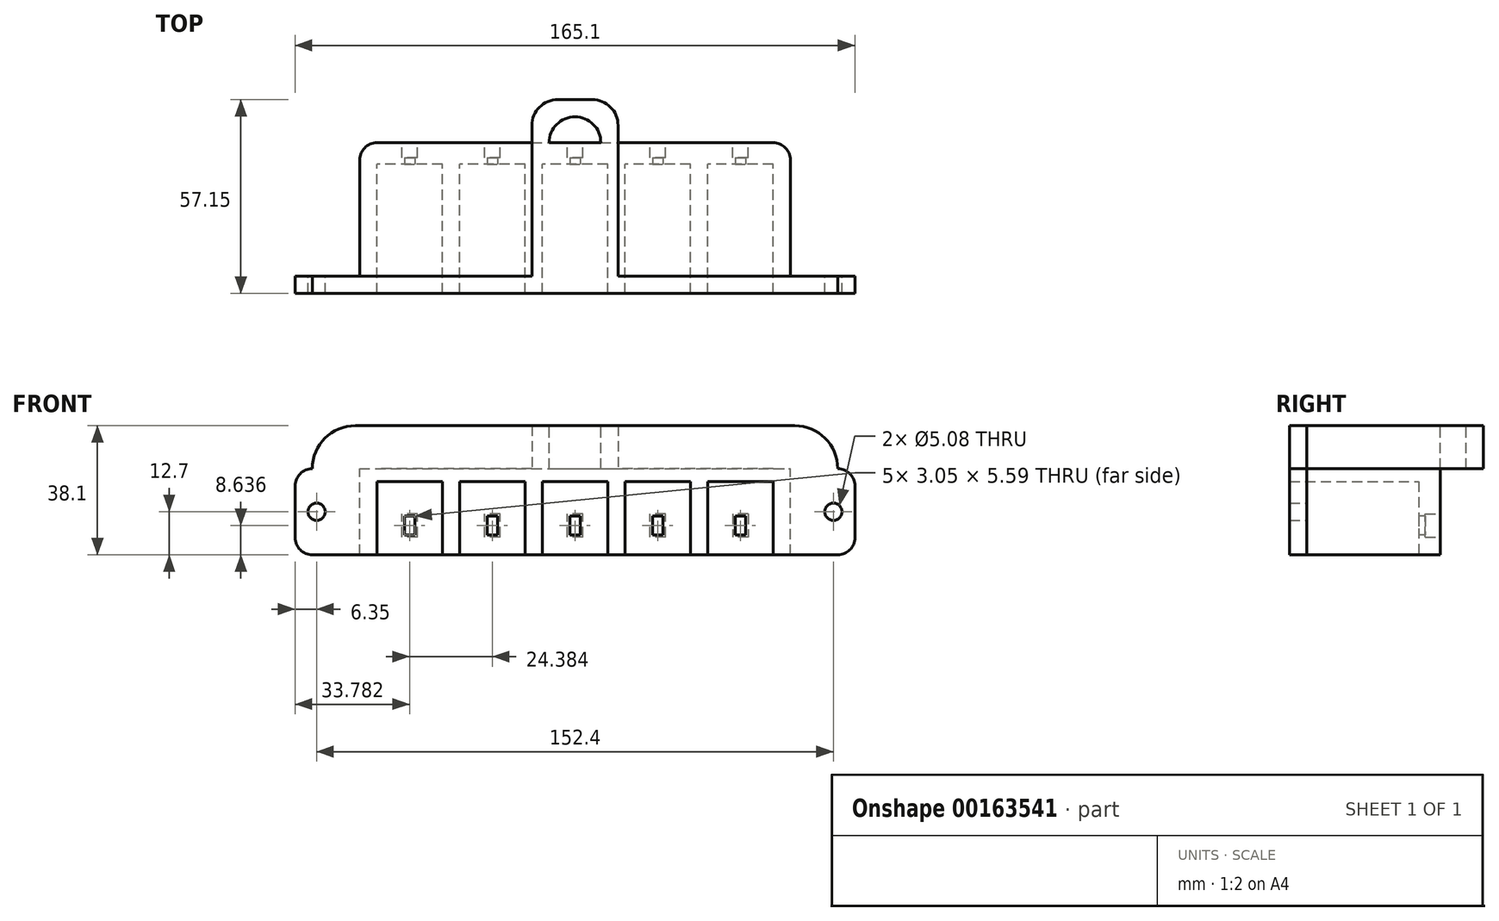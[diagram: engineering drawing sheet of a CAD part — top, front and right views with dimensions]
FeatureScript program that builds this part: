
annotation { "Feature Type Name" : "Feature", "Feature Type Description" : "" }
export const myFeature = defineFeature(function(context is Context, id is Id, definition is map)
    precondition{}
    {
        {
            var Q0;
            Q0=qCreatedBy(makeId("Front.planeOp"),FACE);
            var sketch = newSketch(context, id + "F0", { "sketchPlane" : qUnion([Q0])});
            skLineSegment(sketch, "E0.bottom", {"start": v(0, 0) * mm, "end": v(-127, 0) * mm});
            skLineSegment(sketch, "E0.top", {"start": v(0, 25.4) * mm, "end": v(-127, 25.4) * mm});
            skLineSegment(sketch, "E0.left", {"start": v(0, 0) * mm, "end": v(0, 25.4) * mm});
            skLineSegment(sketch, "E0.right", {"start": v(-127, 0) * mm, "end": v(-127, 25.4) * mm});
            skSolve(sketch);
        }
        {
            var Q0;
            Q0=makeQuery(id+"F0.imprint","IMPRINT",FACE,{"disambiguationData":[TD([[makeQuery(id+"F0.imprint","IMPRINT",EDGE,{"derivedFrom":sQuery(id+"F0.wireOp",EDGE,"E0.bottom")}),-1.0]])]});
            extrude(context, id + "F1", {"entities" : qUnion([Q0]), "depth" : 6.35 * mm});
        }
        {
            var Q0;
            Q0=makeQuery(id+"F1.opExtrude","CAP_FACE",FACE,{"disambiguationData":[OSD([sQuery(id+"F0.wireOp",EDGE,"E0.bottom"),sQuery(id+"F0.wireOp",EDGE,"E0.top"),sQuery(id+"F0.wireOp",EDGE,"E0.left"),sQuery(id+"F0.wireOp",EDGE,"E0.right")])],"isStart":false});
            var sketch = newSketch(context, id + "F2", { "sketchPlane" : qUnion([Q0])});
            skLineSegment(sketch, "E1.bottom", {"start": v(-127, 25.4) * mm, "end": v(-121.92, 25.4) * mm});
            skLineSegment(sketch, "E1.top", {"start": v(-127, 0) * mm, "end": v(-121.92, 0) * mm});
            skLineSegment(sketch, "E1.left", {"start": v(-127, 25.4) * mm, "end": v(-127, 0) * mm});
            skLineSegment(sketch, "E1.right", {"start": v(-121.92, 25.4) * mm, "end": v(-121.92, 0) * mm});
            skLineSegment(sketch, "E2.bottom", {"start": v(-102.62, 25.4) * mm, "end": v(-97.54, 25.4) * mm});
            skLineSegment(sketch, "E2.top", {"start": v(-102.62, 0) * mm, "end": v(-97.54, 0) * mm});
            skLineSegment(sketch, "E2.left", {"start": v(-102.62, 25.4) * mm, "end": v(-102.62, 0) * mm});
            skLineSegment(sketch, "E2.right", {"start": v(-97.54, 25.4) * mm, "end": v(-97.54, 0) * mm});
            skLineSegment(sketch, "E3.bottom", {"start": v(-78.23, 25.4) * mm, "end": v(-73.15, 25.4) * mm});
            skLineSegment(sketch, "E3.top", {"start": v(-78.23, 0) * mm, "end": v(-73.15, 0) * mm});
            skLineSegment(sketch, "E3.left", {"start": v(-78.23, 25.4) * mm, "end": v(-78.23, 0) * mm});
            skLineSegment(sketch, "E3.right", {"start": v(-73.15, 25.4) * mm, "end": v(-73.15, 0) * mm});
            skLineSegment(sketch, "E4.bottom", {"start": v(-53.85, 25.4) * mm, "end": v(-48.77, 25.4) * mm});
            skLineSegment(sketch, "E4.top", {"start": v(-53.85, 0) * mm, "end": v(-48.77, 0) * mm});
            skLineSegment(sketch, "E4.left", {"start": v(-53.85, 25.4) * mm, "end": v(-53.85, 0) * mm});
            skLineSegment(sketch, "E4.right", {"start": v(-48.77, 25.4) * mm, "end": v(-48.77, 0) * mm});
            skLineSegment(sketch, "E5.bottom", {"start": v(-29.46, 25.4) * mm, "end": v(-24.38, 25.4) * mm});
            skLineSegment(sketch, "E5.top", {"start": v(-29.46, 0) * mm, "end": v(-24.38, 0) * mm});
            skLineSegment(sketch, "E5.left", {"start": v(-29.46, 25.4) * mm, "end": v(-29.46, 0) * mm});
            skLineSegment(sketch, "E5.right", {"start": v(-24.38, 25.4) * mm, "end": v(-24.38, 0) * mm});
            skLineSegment(sketch, "E6.bottom", {"start": v(0, 25.4) * mm, "end": v(-5.08, 25.4) * mm});
            skLineSegment(sketch, "E6.top", {"start": v(0, 0) * mm, "end": v(-5.08, 0) * mm});
            skLineSegment(sketch, "E6.left", {"start": v(0, 25.4) * mm, "end": v(0, 0) * mm});
            skLineSegment(sketch, "E6.right", {"start": v(-5.08, 25.4) * mm, "end": v(-5.08, 0) * mm});
            skLineSegment(sketch, "E7.bottom", {"start": v(-5.08, 25.4) * mm, "end": v(-24.38, 25.4) * mm});
            skLineSegment(sketch, "E7.top", {"start": v(-5.08, 21.59) * mm, "end": v(-24.38, 21.59) * mm});
            skLineSegment(sketch, "E7.left", {"start": v(-5.08, 25.4) * mm, "end": v(-5.08, 21.59) * mm});
            skLineSegment(sketch, "E7.right", {"start": v(-24.38, 25.4) * mm, "end": v(-24.38, 21.59) * mm});
            skLineSegment(sketch, "E8.bottom", {"start": v(-29.46, 25.4) * mm, "end": v(-48.77, 25.4) * mm});
            skLineSegment(sketch, "E8.top", {"start": v(-29.46, 21.59) * mm, "end": v(-48.77, 21.59) * mm});
            skLineSegment(sketch, "E8.left", {"start": v(-29.46, 25.4) * mm, "end": v(-29.46, 21.59) * mm});
            skLineSegment(sketch, "E8.right", {"start": v(-48.77, 25.4) * mm, "end": v(-48.77, 21.59) * mm});
            skLineSegment(sketch, "E9.bottom", {"start": v(-53.85, 25.4) * mm, "end": v(-73.15, 25.4) * mm});
            skLineSegment(sketch, "E9.top", {"start": v(-53.85, 21.59) * mm, "end": v(-73.15, 21.59) * mm});
            skLineSegment(sketch, "E9.left", {"start": v(-53.85, 25.4) * mm, "end": v(-53.85, 21.59) * mm});
            skLineSegment(sketch, "E9.right", {"start": v(-73.15, 25.4) * mm, "end": v(-73.15, 21.59) * mm});
            skLineSegment(sketch, "E10.bottom", {"start": v(-78.23, 25.4) * mm, "end": v(-97.54, 25.4) * mm});
            skLineSegment(sketch, "E10.top", {"start": v(-78.23, 21.59) * mm, "end": v(-97.54, 21.59) * mm});
            skLineSegment(sketch, "E10.left", {"start": v(-78.23, 25.4) * mm, "end": v(-78.23, 21.59) * mm});
            skLineSegment(sketch, "E10.right", {"start": v(-97.54, 25.4) * mm, "end": v(-97.54, 21.59) * mm});
            skLineSegment(sketch, "E11.bottom", {"start": v(-102.62, 25.4) * mm, "end": v(-121.92, 25.4) * mm});
            skLineSegment(sketch, "E11.top", {"start": v(-102.62, 21.59) * mm, "end": v(-121.92, 21.59) * mm});
            skLineSegment(sketch, "E11.left", {"start": v(-102.62, 25.4) * mm, "end": v(-102.62, 21.59) * mm});
            skLineSegment(sketch, "E11.right", {"start": v(-121.92, 25.4) * mm, "end": v(-121.92, 21.59) * mm});
            skSolve(sketch);
        }
        {
            var Q0;
            Q0 = qSketchRegion(id + "F2", true);
            extrude(context, id + "F3", {"entities" : qUnion([Q0]), "operationType" : NewBodyOperationType.ADD, "depth" : 38.1 * mm});
        }
        {
            var Q0;
            {var subQ0=sQuery(id+"F0.wireOp",EDGE,"E0.bottom");Q0=makeQuery(id+"F3.boolean.opBoolean","SPLIT",FACE,{"disambiguationData":[TD([makeQuery(id+"F3.opExtrude","SWEPT_FACE",FACE,{"disambiguationData":[OSD([sQuery(id+"F2.wireOp",EDGE,"E5.right")])]})])],"derivedFrom":makeQuery(id+"F1.opExtrude","CAP_FACE",FACE,{"disambiguationData":[OSD([subQ0,sQuery(id+"F0.wireOp",EDGE,"E0.top"),sQuery(id+"F0.wireOp",EDGE,"E0.left"),sQuery(id+"F0.wireOp",EDGE,"E0.right")])],"isStart":false})});}
            var sketch = newSketch(context, id + "F4", { "sketchPlane" : qUnion([Q0])});
            skPoint(sketch, "E12", {"position": v(-14.73, 8.64) * mm});
            skLineSegment(sketch, "E13.bottom", {"start": v(-16.26, 11.43) * mm, "end": v(-13.2, 11.43) * mm});
            skLineSegment(sketch, "E13.top", {"start": v(-16.26, 5.84) * mm, "end": v(-13.2, 5.84) * mm});
            skLineSegment(sketch, "E13.left", {"start": v(-16.26, 11.43) * mm, "end": v(-16.26, 5.84) * mm});
            skLineSegment(sketch, "E13.right", {"start": v(-13.2, 11.43) * mm, "end": v(-13.2, 5.84) * mm});
            skSolve(sketch);
        }
        {
            var Q0;
            Q0 = qSketchRegion(id + "F4", true);
            extrude(context, id + "F5", {"entities" : qUnion([Q0]), "operationType" : NewBodyOperationType.REMOVE, "endBound" : BoundingType.THROUGH_ALL, "oppositeDirection" : true, "depth" : 5.08 * mm});
        }
        {
            var Q0;
            {var subQ0=sQuery(id+"F0.wireOp",EDGE,"E0.bottom");Q0=makeQuery(id+"F3.boolean.opBoolean","SPLIT",FACE,{"disambiguationData":[TD([makeQuery(id+"F3.opExtrude","SWEPT_FACE",FACE,{"disambiguationData":[OSD([sQuery(id+"F2.wireOp",EDGE,"E4.right")])]})])],"derivedFrom":makeQuery(id+"F1.opExtrude","CAP_FACE",FACE,{"disambiguationData":[OSD([subQ0,sQuery(id+"F0.wireOp",EDGE,"E0.top"),sQuery(id+"F0.wireOp",EDGE,"E0.left"),sQuery(id+"F0.wireOp",EDGE,"E0.right")])],"isStart":false})});}
            var sketch = newSketch(context, id + "F6", { "sketchPlane" : qUnion([Q0])});
            skLineSegment(sketch, "E14.bottom", {"start": v(-40.64, 11.43) * mm, "end": v(-37.6, 11.43) * mm});
            skLineSegment(sketch, "E14.top", {"start": v(-40.64, 5.84) * mm, "end": v(-37.6, 5.84) * mm});
            skLineSegment(sketch, "E14.left", {"start": v(-40.64, 11.43) * mm, "end": v(-40.64, 5.84) * mm});
            skLineSegment(sketch, "E14.right", {"start": v(-37.6, 11.43) * mm, "end": v(-37.6, 5.84) * mm});
            skPoint(sketch, "E14.middle", {"position": v(-39.12, 8.64) * mm});
            skLineSegment(sketch, "E15.bottom", {"start": v(-65.02, 11.43) * mm, "end": v(-61.98, 11.43) * mm});
            skLineSegment(sketch, "E15.top", {"start": v(-65.02, 5.84) * mm, "end": v(-61.98, 5.84) * mm});
            skLineSegment(sketch, "E15.left", {"start": v(-65.02, 11.43) * mm, "end": v(-65.02, 5.84) * mm});
            skLineSegment(sketch, "E15.right", {"start": v(-61.98, 11.43) * mm, "end": v(-61.98, 5.84) * mm});
            skPoint(sketch, "E15.middle", {"position": v(-63.5, 8.64) * mm});
            skLineSegment(sketch, "E16.bottom", {"start": v(-89.4, 11.43) * mm, "end": v(-86.36, 11.43) * mm});
            skLineSegment(sketch, "E16.top", {"start": v(-89.4, 5.84) * mm, "end": v(-86.36, 5.84) * mm});
            skLineSegment(sketch, "E16.left", {"start": v(-89.4, 11.43) * mm, "end": v(-89.4, 5.84) * mm});
            skLineSegment(sketch, "E16.right", {"start": v(-86.36, 11.43) * mm, "end": v(-86.36, 5.84) * mm});
            skPoint(sketch, "E16.middle", {"position": v(-87.88, 8.64) * mm});
            skLineSegment(sketch, "E17.bottom", {"start": v(-113.8, 11.43) * mm, "end": v(-110.74, 11.43) * mm});
            skLineSegment(sketch, "E17.top", {"start": v(-113.8, 5.84) * mm, "end": v(-110.74, 5.84) * mm});
            skLineSegment(sketch, "E17.left", {"start": v(-113.8, 11.43) * mm, "end": v(-113.8, 5.84) * mm});
            skLineSegment(sketch, "E17.right", {"start": v(-110.74, 11.43) * mm, "end": v(-110.74, 5.84) * mm});
            skPoint(sketch, "E17.middle", {"position": v(-112.27, 8.64) * mm});
            skSolve(sketch);
        }
        {
            var Q0;
            Q0 = qSketchRegion(id + "F6", true);
            extrude(context, id + "F7", {"entities" : qUnion([Q0]), "operationType" : NewBodyOperationType.REMOVE, "endBound" : BoundingType.THROUGH_ALL, "oppositeDirection" : true, "depth" : 25.4 * mm});
        }
        {
            var Q0;
            Q0=makeQuery(id+"F1.opExtrude","CAP_FACE",FACE,{"disambiguationData":[OSD([sQuery(id+"F0.wireOp",EDGE,"E0.bottom"),sQuery(id+"F0.wireOp",EDGE,"E0.top"),sQuery(id+"F0.wireOp",EDGE,"E0.left"),sQuery(id+"F0.wireOp",EDGE,"E0.right")])],"isStart":true});
            var sketch = newSketch(context, id + "F8", { "sketchPlane" : qUnion([Q0])});
            skLineSegment(sketch, "E18.0", {"start": v(13.2, 11.43) * mm, "end": v(13.2, 5.84) * mm});
            skLineSegment(sketch, "E18.1", {"start": v(16.26, 11.43) * mm, "end": v(16.26, 5.84) * mm});
            skLineSegment(sketch, "E18.2", {"start": v(16.26, 5.84) * mm, "end": v(13.2, 5.84) * mm});
            skLineSegment(sketch, "E18.3", {"start": v(16.26, 11.43) * mm, "end": v(13.2, 11.43) * mm});
            skLineSegment(sketch, "E19.bottom", {"start": v(12.45, 12.07) * mm, "end": v(17.02, 12.07) * mm});
            skLineSegment(sketch, "E19.top", {"start": v(12.45, 5.2) * mm, "end": v(17.02, 5.2) * mm});
            skLineSegment(sketch, "E19.left", {"start": v(12.45, 12.07) * mm, "end": v(12.45, 5.2) * mm});
            skLineSegment(sketch, "E19.right", {"start": v(17.02, 12.07) * mm, "end": v(17.02, 5.2) * mm});
            skPoint(sketch, "E19.middle", {"position": v(14.73, 8.64) * mm});
            skLineSegment(sketch, "E20.0", {"start": v(40.64, 5.84) * mm, "end": v(37.6, 5.84) * mm});
            skLineSegment(sketch, "E20.1", {"start": v(40.64, 11.43) * mm, "end": v(40.64, 5.84) * mm});
            skLineSegment(sketch, "E20.2", {"start": v(40.64, 11.43) * mm, "end": v(37.6, 11.43) * mm});
            skLineSegment(sketch, "E20.3", {"start": v(37.6, 11.43) * mm, "end": v(37.6, 5.84) * mm});
            skLineSegment(sketch, "E21.0", {"start": v(65.02, 11.43) * mm, "end": v(65.02, 5.84) * mm});
            skLineSegment(sketch, "E21.1", {"start": v(65.02, 5.84) * mm, "end": v(61.98, 5.84) * mm});
            skLineSegment(sketch, "E21.2", {"start": v(61.98, 11.43) * mm, "end": v(61.98, 5.84) * mm});
            skLineSegment(sketch, "E21.3", {"start": v(65.02, 11.43) * mm, "end": v(61.98, 11.43) * mm});
            skLineSegment(sketch, "E22.0", {"start": v(89.4, 5.84) * mm, "end": v(86.36, 5.84) * mm});
            skLineSegment(sketch, "E22.1", {"start": v(89.4, 11.43) * mm, "end": v(89.4, 5.84) * mm});
            skLineSegment(sketch, "E22.2", {"start": v(89.4, 11.43) * mm, "end": v(86.36, 11.43) * mm});
            skLineSegment(sketch, "E22.3", {"start": v(86.36, 11.43) * mm, "end": v(86.36, 5.84) * mm});
            skLineSegment(sketch, "E23.0", {"start": v(113.8, 5.84) * mm, "end": v(110.74, 5.84) * mm});
            skLineSegment(sketch, "E23.1", {"start": v(113.8, 11.43) * mm, "end": v(113.8, 5.84) * mm});
            skLineSegment(sketch, "E23.2", {"start": v(113.8, 11.43) * mm, "end": v(110.74, 11.43) * mm});
            skLineSegment(sketch, "E23.3", {"start": v(110.74, 11.43) * mm, "end": v(110.74, 5.84) * mm});
            skLineSegment(sketch, "E24.bottom", {"start": v(109.98, 5.2) * mm, "end": v(114.55, 5.2) * mm});
            skLineSegment(sketch, "E24.top", {"start": v(109.98, 12.06) * mm, "end": v(114.55, 12.06) * mm});
            skLineSegment(sketch, "E24.left", {"start": v(109.98, 5.2) * mm, "end": v(109.98, 12.06) * mm});
            skLineSegment(sketch, "E24.right", {"start": v(114.55, 5.2) * mm, "end": v(114.55, 12.06) * mm});
            skPoint(sketch, "E24.middle", {"position": v(112.27, 8.64) * mm});
            skLineSegment(sketch, "E25.bottom", {"start": v(85.6, 5.2) * mm, "end": v(90.17, 5.2) * mm});
            skLineSegment(sketch, "E25.top", {"start": v(85.6, 12.06) * mm, "end": v(90.17, 12.06) * mm});
            skLineSegment(sketch, "E25.left", {"start": v(85.6, 5.2) * mm, "end": v(85.6, 12.06) * mm});
            skLineSegment(sketch, "E25.right", {"start": v(90.17, 5.2) * mm, "end": v(90.17, 12.06) * mm});
            skPoint(sketch, "E25.middle", {"position": v(87.88, 8.64) * mm});
            skLineSegment(sketch, "E26.bottom", {"start": v(61.21, 5.2) * mm, "end": v(65.79, 5.2) * mm});
            skLineSegment(sketch, "E26.top", {"start": v(61.21, 12.06) * mm, "end": v(65.79, 12.06) * mm});
            skLineSegment(sketch, "E26.left", {"start": v(61.21, 5.2) * mm, "end": v(61.21, 12.06) * mm});
            skLineSegment(sketch, "E26.right", {"start": v(65.79, 5.2) * mm, "end": v(65.79, 12.06) * mm});
            skPoint(sketch, "E26.middle", {"position": v(63.5, 8.64) * mm});
            skLineSegment(sketch, "E27.bottom", {"start": v(36.83, 5.2) * mm, "end": v(41.4, 5.2) * mm});
            skLineSegment(sketch, "E27.top", {"start": v(36.83, 12.06) * mm, "end": v(41.4, 12.06) * mm});
            skLineSegment(sketch, "E27.left", {"start": v(36.83, 5.2) * mm, "end": v(36.83, 12.06) * mm});
            skLineSegment(sketch, "E27.right", {"start": v(41.4, 5.2) * mm, "end": v(41.4, 12.06) * mm});
            skPoint(sketch, "E27.middle", {"position": v(39.12, 8.64) * mm});
            skSolve(sketch);
        }
        {
            var Q0;
            Q0 = qSketchRegion(id + "F8", true);
            extrude(context, id + "F9", {"entities" : qUnion([Q0]), "operationType" : NewBodyOperationType.REMOVE, "oppositeDirection" : true, "depth" : 4.44 * mm});
        }
        {
            var Q0;
            Q0=makeQuery(id+"F3.boolean.opBoolean","MERGE",FACE,{"derivedFrom":[makeQuery(id+"F1.opExtrude","SWEPT_FACE",FACE,{"disambiguationData":[OSD([sQuery(id+"F0.wireOp",EDGE,"E0.left")])]}),makeQuery(id+"F3.opExtrude","SWEPT_FACE",FACE,{"disambiguationData":[OSD([sQuery(id+"F2.wireOp",EDGE,"E6.left")])]})]});
            var sketch = newSketch(context, id + "F10", { "sketchPlane" : qUnion([Q0])});
            skLineSegment(sketch, "E28.bottom", {"start": v(-44.45, 25.4) * mm, "end": v(-39.37, 25.4) * mm});
            skLineSegment(sketch, "E28.top", {"start": v(-44.45, 0) * mm, "end": v(-39.37, 0) * mm});
            skLineSegment(sketch, "E28.left", {"start": v(-44.45, 25.4) * mm, "end": v(-44.45, 0) * mm});
            skLineSegment(sketch, "E28.right", {"start": v(-39.37, 25.4) * mm, "end": v(-39.37, 0) * mm});
            skSolve(sketch);
        }
        {
            var Q0;
            Q0=makeQuery(id+"F10.imprint","IMPRINT",FACE,{"disambiguationData":[TD([[makeQuery(id+"F10.imprint","IMPRINT",EDGE,{"derivedFrom":sQuery(id+"F10.wireOp",EDGE,"E28.bottom")}),-1.0]])]});
            extrude(context, id + "F11", {"entities" : qUnion([Q0]), "operationType" : NewBodyOperationType.ADD, "depth" : 19.05 * mm});
        }
        {
            var Q0;
            Q0=makeQuery(id+"F3.boolean.opBoolean","MERGE",FACE,{"derivedFrom":[makeQuery(id+"F1.opExtrude","SWEPT_FACE",FACE,{"disambiguationData":[OSD([sQuery(id+"F0.wireOp",EDGE,"E0.right")])]}),makeQuery(id+"F3.opExtrude","SWEPT_FACE",FACE,{"disambiguationData":[OSD([sQuery(id+"F2.wireOp",EDGE,"E1.left")])]})]});
            var sketch = newSketch(context, id + "F12", { "sketchPlane" : qUnion([Q0])});
            skLineSegment(sketch, "E29.bottom", {"start": v(44.45, 0) * mm, "end": v(39.37, 0) * mm});
            skLineSegment(sketch, "E29.top", {"start": v(44.45, 25.4) * mm, "end": v(39.37, 25.4) * mm});
            skLineSegment(sketch, "E29.left", {"start": v(44.45, 0) * mm, "end": v(44.45, 25.4) * mm});
            skLineSegment(sketch, "E29.right", {"start": v(39.37, 0) * mm, "end": v(39.37, 25.4) * mm});
            skSolve(sketch);
        }
        {
            var Q0;
            Q0=makeQuery(id+"F12.imprint","IMPRINT",FACE,{"disambiguationData":[TD([[makeQuery(id+"F12.imprint","IMPRINT",EDGE,{"derivedFrom":sQuery(id+"F12.wireOp",EDGE,"E29.bottom")}),-1.0]])]});
            extrude(context, id + "F13", {"entities" : qUnion([Q0]), "operationType" : NewBodyOperationType.ADD, "depth" : 19.05 * mm});
        }
        {
            var Q0;
            Q0=makeQuery(id+"F11.opExtrude","SWEPT_FACE",FACE,{"disambiguationData":[OSD([sQuery(id+"F10.wireOp",EDGE,"E28.right")])]});
            var sketch = newSketch(context, id + "F14", { "sketchPlane" : qUnion([Q0])});
            skCircle(sketch, "E30", {"center": v(-12.7, 12.7) * mm, "radius": 2.54 * mm});
            skPoint(sketch, "E30.centerSnap0", {"position": v(0, 12.7) * mm});
            skCircle(sketch, "E31", {"center": v(139.7, 12.7) * mm, "radius": 2.54 * mm});
            skSolve(sketch);
        }
        {
            var Q0;
            Q0 = qSketchRegion(id + "F14", true);
            extrude(context, id + "F15", {"entities" : qUnion([Q0]), "operationType" : NewBodyOperationType.REMOVE, "endBound" : BoundingType.THROUGH_ALL, "oppositeDirection" : true, "depth" : 25.4 * mm});
        }
        {
            var Q0;
            Q0=makeQuery(id+"F11.opExtrude","CAP_EDGE",EDGE,{"disambiguationData":[OSD([sQuery(id+"F10.wireOp",EDGE,"E28.top")])],"isStart":false});
            var Q1;
            Q1=makeQuery(id+"F11.opExtrude","CAP_EDGE",EDGE,{"disambiguationData":[OSD([sQuery(id+"F10.wireOp",EDGE,"E28.bottom")])],"isStart":false});
            var Q2;
            Q2=makeQuery(id+"F13.opExtrude","CAP_EDGE",EDGE,{"disambiguationData":[OSD([sQuery(id+"F12.wireOp",EDGE,"E29.bottom")])],"isStart":false});
            var Q3;
            Q3=makeQuery(id+"F13.opExtrude","CAP_EDGE",EDGE,{"disambiguationData":[OSD([sQuery(id+"F12.wireOp",EDGE,"E29.top")])],"isStart":false});
            var Q4;
            Q4=makeQuery(id+"F1.opExtrude","CAP_EDGE",EDGE,{"disambiguationData":[OSD([sQuery(id+"F0.wireOp",EDGE,"E0.right")])],"isStart":true});
            var Q5;
            Q5=makeQuery(id+"F1.opExtrude","CAP_EDGE",EDGE,{"disambiguationData":[OSD([sQuery(id+"F0.wireOp",EDGE,"E0.left")])],"isStart":true});
            fillet(context, id + "F16", {"entities" : qUnion([Q0, Q1, Q2, Q3, Q4, Q5]), "radius" : 5.08 * mm, "tangentPropagation" : true, "allowEdgeOverflow" : false});
        }
        {
            var Q0;
            Q0=makeQuery(id+"F13.boolean.opBoolean","MERGE",FACE,{"derivedFrom":[makeQuery(id+"F11.boolean.opBoolean","MERGE",FACE,{"derivedFrom":[makeQuery(id+"F3.boolean.opBoolean","MERGE",FACE,{"derivedFrom":[makeQuery(id+"F1.opExtrude","SWEPT_FACE",FACE,{"disambiguationData":[OSD([sQuery(id+"F0.wireOp",EDGE,"E0.top")])]}),makeQuery(id+"F3.opExtrude","SWEPT_FACE",FACE,{"disambiguationData":[OSD([sQuery(id+"F2.wireOp",EDGE,"E1.bottom"),sQuery(id+"F2.wireOp",EDGE,"E2.bottom"),sQuery(id+"F2.wireOp",EDGE,"E3.bottom"),sQuery(id+"F2.wireOp",EDGE,"E4.bottom"),sQuery(id+"F2.wireOp",EDGE,"E5.bottom"),sQuery(id+"F2.wireOp",EDGE,"E6.bottom"),sQuery(id+"F2.wireOp",EDGE,"E7.bottom"),sQuery(id+"F2.wireOp",EDGE,"E8.bottom"),sQuery(id+"F2.wireOp",EDGE,"E9.bottom"),sQuery(id+"F2.wireOp",EDGE,"E10.bottom"),sQuery(id+"F2.wireOp",EDGE,"E11.bottom")])]})]}),makeQuery(id+"F11.opExtrude","SWEPT_FACE",FACE,{"disambiguationData":[OSD([sQuery(id+"F10.wireOp",EDGE,"E28.bottom")])]})]}),makeQuery(id+"F13.opExtrude","SWEPT_FACE",FACE,{"disambiguationData":[OSD([sQuery(id+"F12.wireOp",EDGE,"E29.top")])]})]});
            var sketch = newSketch(context, id + "F17", { "sketchPlane" : qUnion([Q0])});
            skLineSegment(sketch, "E32.bottom", {"start": v(-140.97, -39.37) * mm, "end": v(13.97, -39.37) * mm});
            skLineSegment(sketch, "E32.top", {"start": v(-140.97, -44.45) * mm, "end": v(13.97, -44.45) * mm});
            skLineSegment(sketch, "E32.left", {"start": v(-140.97, -39.37) * mm, "end": v(-140.97, -44.45) * mm});
            skLineSegment(sketch, "E32.right", {"start": v(13.97, -39.37) * mm, "end": v(13.97, -44.45) * mm});
            skSolve(sketch);
        }
        {
            var Q0;
            Q0 = qSketchRegion(id + "F17", true);
            extrude(context, id + "F18", {"entities" : qUnion([Q0]), "operationType" : NewBodyOperationType.ADD, "depth" : 12.7 * mm});
        }
        {
            var Q0;
            Q0=makeQuery(id+"F18.opExtrude","CAP_EDGE",EDGE,{"disambiguationData":[OSD([sQuery(id+"F17.wireOp",EDGE,"E32.right")])],"isStart":false});
            var Q1;
            Q1=makeQuery(id+"F18.opExtrude","CAP_EDGE",EDGE,{"disambiguationData":[OSD([sQuery(id+"F17.wireOp",EDGE,"E32.left")])],"isStart":false});
            fillet(context, id + "F19", {"entities" : qUnion([Q0, Q1]), "radius" : 12.7 * mm, "tangentPropagation" : true, "allowEdgeOverflow" : false});
        }
        {
            var Q0;
            Q0=makeQuery(id+"F13.boolean.opBoolean","MERGE",FACE,{"derivedFrom":[makeQuery(id+"F11.boolean.opBoolean","MERGE",FACE,{"derivedFrom":[makeQuery(id+"F3.boolean.opBoolean","MERGE",FACE,{"derivedFrom":[makeQuery(id+"F1.opExtrude","SWEPT_FACE",FACE,{"disambiguationData":[OSD([sQuery(id+"F0.wireOp",EDGE,"E0.top")])]}),makeQuery(id+"F3.opExtrude","SWEPT_FACE",FACE,{"disambiguationData":[OSD([sQuery(id+"F2.wireOp",EDGE,"E1.bottom"),sQuery(id+"F2.wireOp",EDGE,"E2.bottom"),sQuery(id+"F2.wireOp",EDGE,"E3.bottom"),sQuery(id+"F2.wireOp",EDGE,"E4.bottom"),sQuery(id+"F2.wireOp",EDGE,"E5.bottom"),sQuery(id+"F2.wireOp",EDGE,"E6.bottom"),sQuery(id+"F2.wireOp",EDGE,"E7.bottom"),sQuery(id+"F2.wireOp",EDGE,"E8.bottom"),sQuery(id+"F2.wireOp",EDGE,"E9.bottom"),sQuery(id+"F2.wireOp",EDGE,"E10.bottom"),sQuery(id+"F2.wireOp",EDGE,"E11.bottom")])]})]}),makeQuery(id+"F11.opExtrude","SWEPT_FACE",FACE,{"disambiguationData":[OSD([sQuery(id+"F10.wireOp",EDGE,"E28.bottom")])]})]}),makeQuery(id+"F13.opExtrude","SWEPT_FACE",FACE,{"disambiguationData":[OSD([sQuery(id+"F12.wireOp",EDGE,"E29.top")])]})]});
            var sketch = newSketch(context, id + "F20", { "sketchPlane" : qUnion([Q0])});
            skLineSegment(sketch, "E33.bottom", {"start": v(-76.2, -39.37) * mm, "end": v(-50.8, -39.37) * mm});
            skLineSegment(sketch, "E33.top", {"start": v(-76.2, 0) * mm, "end": v(-50.8, 0) * mm});
            skLineSegment(sketch, "E33.left", {"start": v(-76.2, -39.37) * mm, "end": v(-76.2, 0) * mm});
            skLineSegment(sketch, "E33.right", {"start": v(-50.8, -39.37) * mm, "end": v(-50.8, 0) * mm});
            skSolve(sketch);
        }
        {
            var Q0;
            Q0 = qSketchRegion(id + "F20", true);
            extrude(context, id + "F21", {"entities" : qUnion([Q0]), "operationType" : NewBodyOperationType.ADD, "depth" : 12.7 * mm});
        }
        {
            var Q0;
            Q0=makeQuery(id+"F21.boolean.opBoolean","MERGE",FACE,{"derivedFrom":[makeQuery(id+"F1.opExtrude","CAP_FACE",FACE,{"disambiguationData":[OSD([sQuery(id+"F0.wireOp",EDGE,"E0.bottom"),sQuery(id+"F0.wireOp",EDGE,"E0.top"),sQuery(id+"F0.wireOp",EDGE,"E0.left"),sQuery(id+"F0.wireOp",EDGE,"E0.right")])],"isStart":true}),makeQuery(id+"F21.opExtrude","SWEPT_FACE",FACE,{"disambiguationData":[OSD([sQuery(id+"F20.wireOp",EDGE,"E33.top")])]})]});
            var sketch = newSketch(context, id + "F22", { "sketchPlane" : qUnion([Q0])});
            skLineSegment(sketch, "E34.bottom", {"start": v(76.2, 38.1) * mm, "end": v(50.8, 38.1) * mm});
            skLineSegment(sketch, "E34.top", {"start": v(76.2, 25.4) * mm, "end": v(50.8, 25.4) * mm});
            skLineSegment(sketch, "E34.left", {"start": v(76.2, 38.1) * mm, "end": v(76.2, 25.4) * mm});
            skLineSegment(sketch, "E34.right", {"start": v(50.8, 38.1) * mm, "end": v(50.8, 25.4) * mm});
            skSolve(sketch);
        }
        {
            var Q0;
            Q0 = qSketchRegion(id + "F22", true);
            extrude(context, id + "F23", {"entities" : qUnion([Q0]), "operationType" : NewBodyOperationType.ADD, "depth" : 12.7 * mm});
        }
        {
            var Q0;
            Q0=makeQuery(id+"F23.boolean.opBoolean","MERGE",FACE,{"derivedFrom":[makeQuery(id+"F21.boolean.opBoolean","MERGE",FACE,{"derivedFrom":[makeQuery(id+"F18.opExtrude","CAP_FACE",FACE,{"disambiguationData":[OSD([sQuery(id+"F17.wireOp",EDGE,"E32.bottom"),sQuery(id+"F17.wireOp",EDGE,"E32.top"),sQuery(id+"F17.wireOp",EDGE,"E32.left"),sQuery(id+"F17.wireOp",EDGE,"E32.right")])],"isStart":false}),makeQuery(id+"F21.opExtrude","CAP_FACE",FACE,{"disambiguationData":[OSD([sQuery(id+"F20.wireOp",EDGE,"E33.bottom"),sQuery(id+"F20.wireOp",EDGE,"E33.top"),sQuery(id+"F20.wireOp",EDGE,"E33.left"),sQuery(id+"F20.wireOp",EDGE,"E33.right")])],"isStart":false})]}),makeQuery(id+"F23.opExtrude","SWEPT_FACE",FACE,{"disambiguationData":[OSD([sQuery(id+"F22.wireOp",EDGE,"E34.bottom")])]})]});
            var sketch = newSketch(context, id + "F24", { "sketchPlane" : qUnion([Q0])});
            skArc(sketch, "E35", {"start": v(-71.12, 0) * mm, "mid": v(-63.5, 7.62) * mm, "end": v(-55.88, 0) * mm});
            skLineSegment(sketch, "E36", {"start": v(-71.12, 0) * mm, "end": v(-55.88, 0) * mm});
            skSolve(sketch);
        }
        {
            var Q0;
            Q0 = qSketchRegion(id + "F24", true);
            extrude(context, id + "F25", {"entities" : qUnion([Q0]), "operationType" : NewBodyOperationType.REMOVE, "endBound" : BoundingType.THROUGH_ALL, "oppositeDirection" : true, "depth" : 25.4 * mm});
        }
        {
            var Q0;
            Q0=makeQuery(id+"F23.opExtrude","CAP_EDGE",EDGE,{"disambiguationData":[OSD([sQuery(id+"F22.wireOp",EDGE,"E34.right")])],"isStart":false});
            var Q1;
            Q1=makeQuery(id+"F23.opExtrude","CAP_EDGE",EDGE,{"disambiguationData":[OSD([sQuery(id+"F22.wireOp",EDGE,"E34.left")])],"isStart":false});
            fillet(context, id + "F26", {"entities" : qUnion([Q0, Q1]), "radius" : 7.62 * mm, "tangentPropagation" : true, "allowEdgeOverflow" : false});
        }
    });
